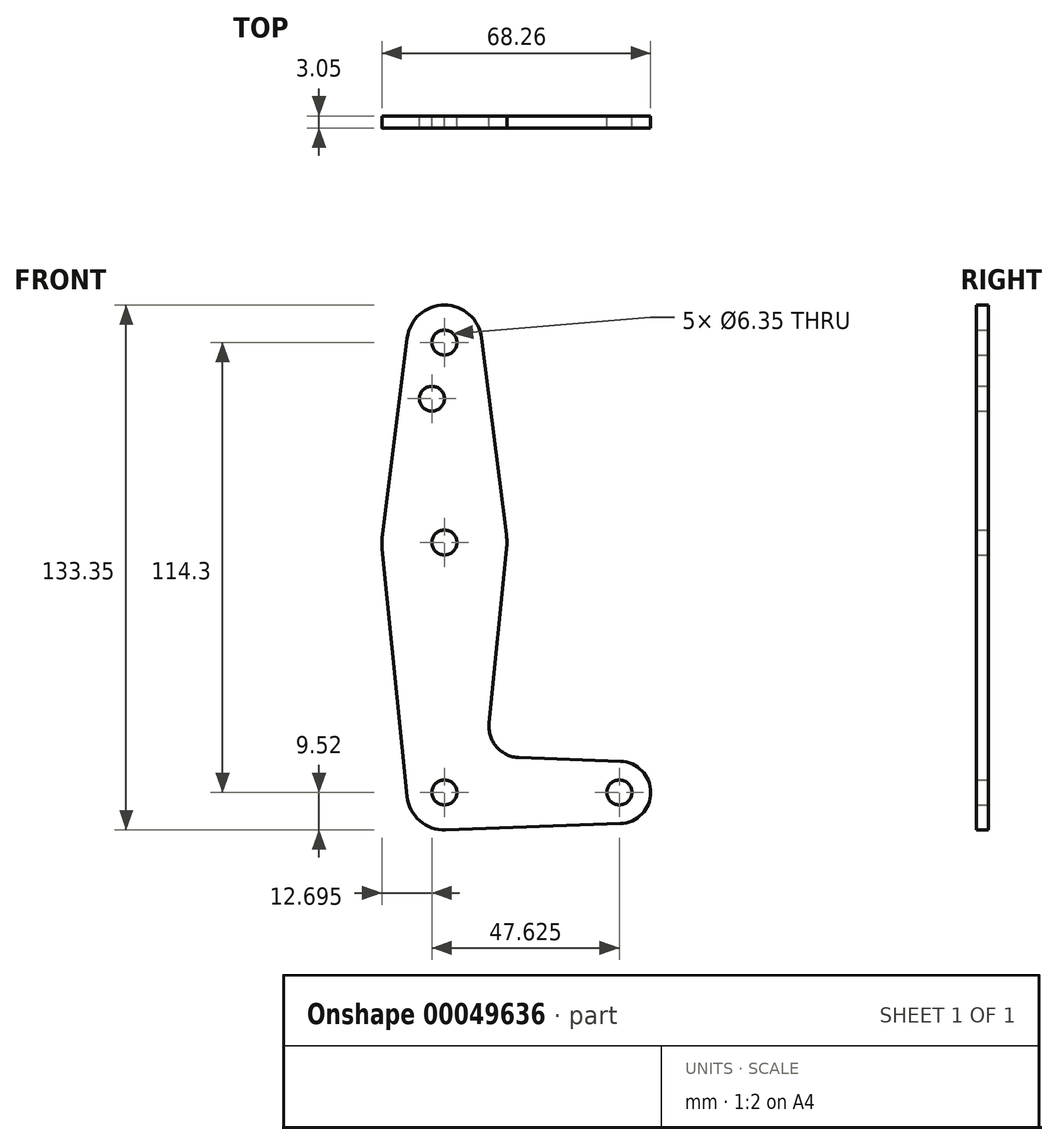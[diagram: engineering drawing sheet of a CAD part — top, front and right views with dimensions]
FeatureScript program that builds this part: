
annotation { "Feature Type Name" : "Feature", "Feature Type Description" : "" }
export const myFeature = defineFeature(function(context is Context, id is Id, definition is map)
    precondition{}
    {
        {
            var Q0;
            Q0=qCreatedBy(makeId("Front.planeOp"),FACE);
            var sketch = newSketch(context, id + "F0", { "sketchPlane" : qUnion([Q0])});
            skCircle(sketch, "E0", {"center": v(0, 0) * mm, "radius": 9.53 * mm});
            skLineSegment(sketch, "E1", {"start": v(0, 0) * mm, "end": v(44.45, 0) * mm, "construction": true});
            skLineSegment(sketch, "E2", {"start": v(0, 0) * mm, "end": v(0, 114.3) * mm, "construction": true});
            skCircle(sketch, "E3", {"center": v(0, 63.5) * mm, "radius": 15.88 * mm});
            skCircle(sketch, "E4", {"center": v(0, 114.3) * mm, "radius": 9.53 * mm});
            skCircle(sketch, "E5", {"center": v(44.45, 0) * mm, "radius": 7.94 * mm});
            skLineSegment(sketch, "E6", {"start": v(9.45, 115.5) * mm, "end": v(15.75, 65.48) * mm});
            skLineSegment(sketch, "E7", {"start": v(15.8, 61.91) * mm, "end": v(11.34, 17.6) * mm});
            skPoint(sketch, "E7.startSnap0", {"position": v(0, 57.15) * mm});
            skLineSegment(sketch, "E8", {"start": v(-9.45, 115.5) * mm, "end": v(-15.75, 65.48) * mm});
            skLineSegment(sketch, "E9", {"start": v(-15.8, 61.91) * mm, "end": v(-9.48, -0.95) * mm});
            skLineSegment(sketch, "E10", {"start": v(18.97, 8.85) * mm, "end": v(44.73, 7.93) * mm});
            skLineSegment(sketch, "E11", {"start": v(0.34, -9.52) * mm, "end": v(44.73, -7.93) * mm});
            skCircle(sketch, "E12", {"center": v(0, 114.3) * mm, "radius": 3.18 * mm});
            skCircle(sketch, "E13", {"center": v(0, 63.5) * mm, "radius": 3.18 * mm});
            skCircle(sketch, "E14", {"center": v(0, 0) * mm, "radius": 3.18 * mm});
            skCircle(sketch, "E15", {"center": v(44.45, 0) * mm, "radius": 3.18 * mm});
            skCircle(sketch, "E16", {"center": v(-3.18, 100.03) * mm, "radius": 3.18 * mm});
            skArc(sketch, "E17.filletArc", {"start": v(11.34, 17.6) * mm, "mid": v(13.26, 11.57) * mm, "end": v(18.97, 8.85) * mm});
            skSolve(sketch);
        }
        {
            var Q0;
            Q0 = qSketchRegion(id + "F0", true);
            extrude(context, id + "F1", {"entities" : qUnion([Q0]), "depth" : 3.05 * mm});
        }
    });
